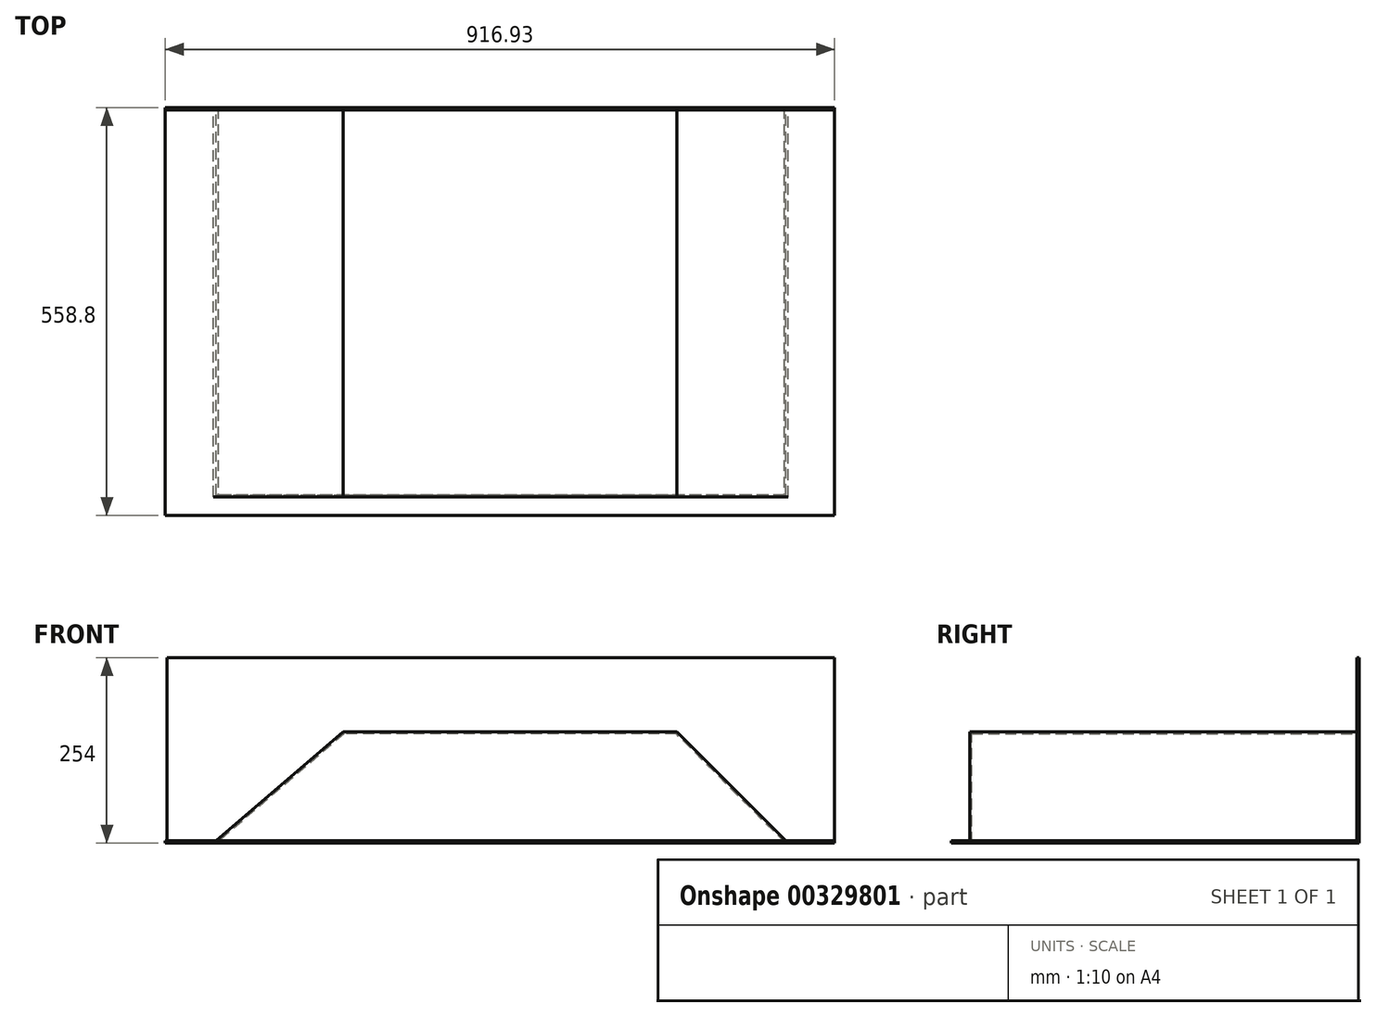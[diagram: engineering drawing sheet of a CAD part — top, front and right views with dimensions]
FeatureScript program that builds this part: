
annotation { "Feature Type Name" : "Feature", "Feature Type Description" : "" }
export const myFeature = defineFeature(function(context is Context, id is Id, definition is map)
    precondition{}
    {
        {
            var Q0;
            Q0=qCreatedBy(makeId("Front.planeOp"),FACE);
            var sketch = newSketch(context, id + "F0", { "sketchPlane" : qUnion([Q0])});
            skLineSegment(sketch, "E0.bottom", {"start": v(0, 0) * mm, "end": v(-914.4, 0) * mm});
            skLineSegment(sketch, "E0.top", {"start": v(0, 254) * mm, "end": v(-914.4, 254) * mm});
            skLineSegment(sketch, "E0.left", {"start": v(0, 0) * mm, "end": v(0, 254) * mm});
            skLineSegment(sketch, "E0.right", {"start": v(-914.4, 0) * mm, "end": v(-914.4, 254) * mm});
            skLineSegment(sketch, "E1.top", {"start": v(-673.1, 152.4) * mm, "end": v(-215.9, 152.4) * mm});
            skLineSegment(sketch, "E1.left", {"start": v(-850.9, 0) * mm, "end": v(-673.1, 152.4) * mm});
            skLineSegment(sketch, "E1.right", {"start": v(-63.5, 0) * mm, "end": v(-215.9, 152.4) * mm});
            skSolve(sketch);
        }
        {
            var Q0;
            Q0=makeQuery(id+"F0.imprint","IMPRINT",FACE,{"disambiguationData":[TD([[makeQuery(id+"F0.imprint","IMPRINT",EDGE,{"derivedFrom":sQuery(id+"F0.wireOp",EDGE,"E0.top")}),1.0]])]});
            extrude(context, id + "F1", {"entities" : qUnion([Q0]), "depth" : 3.17 * mm});
        }
        {
            var Q0;
            Q0=makeQuery(id+"F0.imprint","IMPRINT",FACE,{"disambiguationData":[TD([[makeQuery(id+"F0.imprint","IMPRINT",EDGE,{"derivedFrom":sQuery(id+"F0.wireOp",EDGE,"E1.top")}),-1.0]])]});
            extrude(context, id + "F2", {"entities" : qUnion([Q0]), "operationType" : NewBodyOperationType.ADD, "depth" : 533.4 * mm, "hasSecondDirection" : true, "secondDirectionOppositeDirection" : false, "secondDirectionDepth" : 3.05 * mm});
        }
        {
            var Q0;
            Q0=makeQuery(id+"F2.opExtrude","SWEPT_FACE",FACE,{"disambiguationData":[OSD([sQuery(id+"F0.wireOp",EDGE,"E0.bottom")])]});
            var Q1;
            Q1=makeQuery(id+"F2.opExtrude","CAP_FACE",FACE,{"disambiguationData":[OSD([sQuery(id+"F0.wireOp",EDGE,"E0.bottom"),sQuery(id+"F0.wireOp",EDGE,"E1.top"),sQuery(id+"F0.wireOp",EDGE,"E1.left"),sQuery(id+"F0.wireOp",EDGE,"E1.right")])],"isStart":true});
            shell(context, id + "F3", {"entities" : qUnion([Q0, Q1]), "thickness" : 2.54 * mm});
        }
        {
            var Q0;
            Q0=qCreatedBy(makeId("Top.planeOp"),FACE);
            var sketch = newSketch(context, id + "F4", { "sketchPlane" : qUnion([Q0])});
            skLineSegment(sketch, "E2.bottom", {"start": v(0, 0) * mm, "end": v(-69.1, 0) * mm});
            skLineSegment(sketch, "E2.top", {"start": v(0, -558.8) * mm, "end": v(-916.93, -558.8) * mm});
            skLineSegment(sketch, "E2.left", {"start": v(0, 0) * mm, "end": v(0, -558.8) * mm});
            skLineSegment(sketch, "E2.right", {"start": v(-916.93, 0) * mm, "end": v(-916.93, -558.8) * mm});
            skLineSegment(sketch, "E3.top", {"start": v(-69.1, -530.93) * mm, "end": v(-844.73, -530.93) * mm});
            skLineSegment(sketch, "E3.left", {"start": v(-69.1, 0) * mm, "end": v(-69.1, -530.93) * mm});
            skLineSegment(sketch, "E3.right", {"start": v(-844.73, 0) * mm, "end": v(-844.73, -530.93) * mm});
            skLineSegment(sketch, "E4.trimOffspring", {"start": v(-844.73, 0) * mm, "end": v(-916.93, 0) * mm});
            skSolve(sketch);
        }
        {
            var Q0;
            Q0=makeQuery(id+"F4.imprint","IMPRINT",FACE,{"disambiguationData":[TD([[makeQuery(id+"F4.imprint","IMPRINT",EDGE,{"derivedFrom":sQuery(id+"F4.wireOp",EDGE,"E2.bottom")}),1.0]])]});
            extrude(context, id + "F5", {"entities" : qUnion([Q0]), "depth" : 3.17 * mm});
        }
    });
